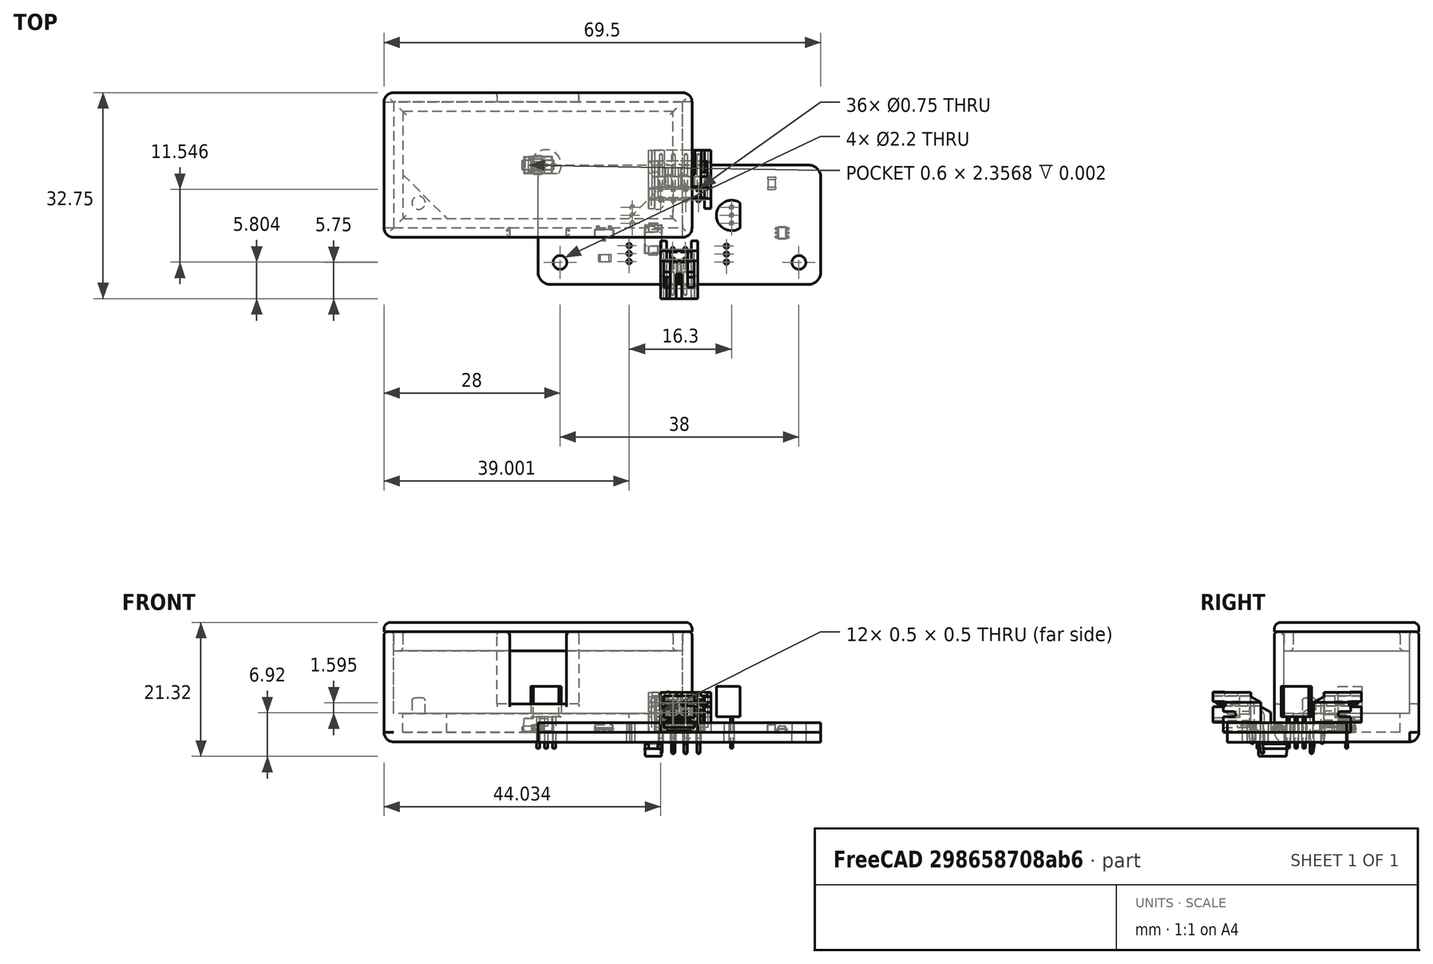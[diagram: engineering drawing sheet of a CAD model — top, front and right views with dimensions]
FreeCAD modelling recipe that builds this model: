
FCSTD DOCUMENT  (FreeCAD 1.0R39319 (Git))
Label: Test2
License: All rights reserved
LicenseURL: https://en.wikipedia.org/wiki/All_rights_reserved
objects: App::Link×31, Part::Feature×18, Sketcher::SketchObject×10, PartDesign::Fillet×8, PartDesign::Pad×6, App::Part×5, PartDesign::Pocket×3, PartDesign::Body×2, Mesh::Feature×2, PartDesign::Thickness×1, PartDesign::CoordinateSystem×1, PartDesign::ShapeBinder×1, App::LinkGroup×1
note: 96 computed .brp shape members not serialized (recipe doc carries the construction recipe); baked Part::Feature solids carry a one-line shape summary decoded from their .brp

FEATURE [Sketcher::SketchObject] Sketch
  ArcFitTolerance = 1e-06
  AttachmentSupport = -> [XY_Plane]
  FullyConstrained = true
  MakeInternals = false
  MapMode = 5
  sketch-geometry (4):
    g0: LineSegment StartX=-23 StartY=10 StartZ=0 EndX=-23 EndY=-10 EndZ=0
    g1: LineSegment StartX=-23 StartY=-10 StartZ=0 EndX=23 EndY=-10 EndZ=0
    g2: LineSegment StartX=23 StartY=-10 StartZ=0 EndX=23 EndY=10 EndZ=0
    g3: LineSegment StartX=23 StartY=10 StartZ=0 EndX=-23 EndY=10 EndZ=0
  constraints (11):
    c: Coincident(g0,g1)
    c: Coincident(g1,g2)
    c: Coincident(g2,g3)
    c: Coincident(g3,g0)
    c: Vertical(g0)
    c: Vertical(g2)
    c: Horizontal(g1)
    c: Horizontal(g3)
    c: Distance(g0,g2) = 46
    c: Distance(g1,g3) = 20
    c: Symmetric(g0,g1,g-1)
FEATURE [PartDesign::Pad] Pad  label="Gehäuse"
  Direction = (0,0,1)
  Length = 16
  Length2 = 10
  Profile = -> Sketch
  ReferenceAxis = -> Sketch [N_Axis]
  Refine = true
  Suppressed = false
  Type = 0
FEATURE [PartDesign::Thickness] Thickness
  Base = -> Pad [Face6]
  BaseFeature = -> Pad
  Intersection = false
  Join = 0
  Mode = 0
  Refine = true
  SupportTransform = false
  Suppressed = false
  Value = 1.5
FEATURE [PartDesign::CoordinateSystem] Local_CS_144d
  AttacherType = Attacher::AttachEngine3D
  MapMode = 2
FEATURE [Part::Feature] Pcb_144d
  Placement = pos=(-88.4,49.6,0) rot=(0,0,1;0rad)
  shape: bbox 45 x 19 x 1.6 mm, 30 faces (baked)
FEATURE [Sketcher::SketchObject] PCB_Sketch_144d
  ArcFitTolerance = 1e-06
  FullyConstrained = false
  MakeInternals = false
  sketch-geometry (8):
    g0: LineSegment StartX=45 StartY=-2 StartZ=0 EndX=45 EndY=-17 EndZ=0
    g1: LineSegment StartX=2 StartY=0 StartZ=0 EndX=43 EndY=0 EndZ=0
    g2: LineSegment StartX=4e-16 StartY=-17 StartZ=0 EndX=0 EndY=-2 EndZ=0
    g3: LineSegment StartX=43 StartY=-19 StartZ=0 EndX=2 EndY=-19 EndZ=0
    g4: ArcOfCircle CenterX=2 CenterY=-17 CenterZ=0 NormalX=0 NormalY=0 NormalZ=-1 AngleXU=-1.5708 Radius=2 StartAngle=0 EndAngle=1.5708
    g5: ArcOfCircle CenterX=2 CenterY=-2 CenterZ=0 NormalX=0 NormalY=0 NormalZ=-1 AngleXU=-7.47076e-07 Radius=2 StartAngle=0 EndAngle=1.5708
    g6: ArcOfCircle CenterX=43 CenterY=-17 CenterZ=0 NormalX=0 NormalY=0 NormalZ=-1 AngleXU=3.14159 Radius=2 StartAngle=0 EndAngle=1.5708
    g7: ArcOfCircle CenterX=43 CenterY=-2 CenterZ=0 NormalX=0 NormalY=0 NormalZ=-1 AngleXU=1.5708 Radius=2 StartAngle=0 EndAngle=1.5708
  constraints (8):
    c: Coincident(g2,g4)
    c: Coincident(g2,g5)
    c: Coincident(g3,g4)
    c: Coincident(g1,g5)
    c: Coincident(g3,g6)
    c: Coincident(g1,g7)
    c: Coincident(g0,g6)
    c: Coincident(g0,g7)
FEATURE [App::Part] Board_Geoms_144d
  Group = -> [Pcb_144d,PCB_Sketch_144d]
  Origin = -> Origin001
FEATURE [Part::Feature] Shape  label="C3_C_0805_2012Metric_59d8a5b28aa1"
  Placement = pos=(37.1791,-2.90075,0) rot=(0,0,-1;1.5708rad)
  shape: bbox 1.25 x 2 x 1.25 mm, 28 faces (baked)
FEATURE [Part::Feature] Shape001  label="Qr1_TO-92_Inline_Narrow_4c17e51feb58"
  Placement = pos=(30.8,-9.3,0) rot=(0,0,1;1.5708rad)
  shape: bbox 3.745 x 4.83 x 9.8 mm, 19 faces (baked)
FEATURE [Part::Feature] Shape002  label="R13_R_0805_2012Metric_05bb72eddab1"
  Placement = pos=(10.6384,-14.7978,0) rot=(0,0,1;0rad)
  shape: bbox 2 x 1.2 x 0.45 mm, 26 faces (baked)
FEATURE [App::Link] R13_R_0805_2012Metric_05bb72eddab1_ln_  label="R12_R_0805_2012Metric_2ca491163d3f"
  LinkPlacement = pos=(41.5,-7.05646,0) rot=(0,0,1;3.14159rad)
  LinkedObject = -> Shape002
  Placement = pos=(41.5,-7.05646,0) rot=(0,0,1;3.14159rad)
FEATURE [App::Link] R13_R_0805_2012Metric_05bb72eddab1_ln_001  label="R7_R_0805_2012Metric_16cffab84ef1"
  LinkPlacement = pos=(6.4,-7.5,0) rot=(0,0,1;1.5708rad)
  LinkedObject = -> Shape002
  Placement = pos=(6.4,-7.5,0) rot=(0,0,1;1.5708rad)
FEATURE [App::Link] R13_R_0805_2012Metric_05bb72eddab1_ln_002  label="R11_R_0805_2012Metric_7a0705619217"
  LinkPlacement = pos=(3.5,-7.1,0) rot=(0,0,1;0rad)
  LinkedObject = -> Shape002
  Placement = pos=(3.5,-7.1,0) rot=(0,0,1;0rad)
FEATURE [Part::Feature] Shape003  label="J2_JST_S2B_PH_K_70a5548a03dd"
  Placement = pos=(21.4384,-13.3978,0) rot=(0,0,1;0rad)
  shape: bbox 5.9 x 7.6 x 8.25 mm, 110 faces (baked)
FEATURE [App::Link] C3_C_0805_2012Metric_59d8a5b28aa1_ln_  label="C4_C_0805_2012Metric_db03d5f05126"
  LinkPlacement = pos=(41.6791,-2.90075,0) rot=(0,0,-1;1.5708rad)
  LinkedObject = -> Shape
  Placement = pos=(41.6791,-2.90075,0) rot=(0,0,-1;1.5708rad)
FEATURE [Part::Feature] Shape004  label="D1_SOT-23_6e08a76b6de6"
  Placement = pos=(10.5,-10.8978,0) rot=(0,0,-1;1.5708rad)
  shape: bbox 3 x 2.5 x 1.2 mm, 69 faces (baked)
FEATURE [App::Link] R13_R_0805_2012Metric_05bb72eddab1_ln_003  label="R1_R_0805_2012Metric_524cef724ac0"
  LinkPlacement = pos=(5.02083,-2.90344,0) rot=(0,0,-1;1.5708rad)
  LinkedObject = -> Shape002
  Placement = pos=(5.02083,-2.90344,0) rot=(0,0,-1;1.5708rad)
FEATURE [App::Link] R13_R_0805_2012Metric_05bb72eddab1_ln_004  label="R14_R_0805_2012Metric_7cf8be774751"
  LinkPlacement = pos=(34.7,-14.8,0) rot=(0,0,1;0rad)
  LinkedObject = -> Shape002
  Placement = pos=(34.7,-14.8,0) rot=(0,0,1;0rad)
FEATURE [App::Link] Qr1_TO_92_Inline_Narrow_4c17e51feb58_ln_  label="Ql1_TO-92_Inline_Narrow_06a0bbdb9195"
  LinkPlacement = pos=(15,-9.3,0) rot=(0,0,1;1.5708rad)
  LinkedObject = -> Shape001
  Placement = pos=(15,-9.3,0) rot=(0,0,1;1.5708rad)
FEATURE [App::Link] R13_R_0805_2012Metric_05bb72eddab1_ln_005  label="R10_R_0805_2012Metric_43a2ade0cd3b"
  LinkPlacement = pos=(38.6,-7.4,0) rot=(0,0,1;1.5708rad)
  LinkedObject = -> Shape002
  Placement = pos=(38.6,-7.4,0) rot=(0,0,1;1.5708rad)
FEATURE [Part::Feature] Shape005  label="Q2_SOT-363_SC-70-6_a433c7552343"
  Placement = pos=(38.8384,-10.7978,0) rot=(0,0,1;0rad)
  shape: bbox 2.1 x 2 x 1.05 mm, 111 faces (baked)
FEATURE [App::Link] R13_R_0805_2012Metric_05bb72eddab1_ln_006  label="R5_R_0805_2012Metric_740ab295292b"
  LinkPlacement = pos=(34.9791,-2.93075,0) rot=(0,0,-1;1.5708rad)
  LinkedObject = -> Shape002
  Placement = pos=(34.9791,-2.93075,0) rot=(0,0,-1;1.5708rad)
FEATURE [App::Link] R13_R_0805_2012Metric_05bb72eddab1_ln_007  label="R8_R_0805_2012Metric_f95ea44c56ff"
  LinkPlacement = pos=(9.3,-7.05784,0) rot=(0,0,1;0rad)
  LinkedObject = -> Shape002
  Placement = pos=(9.3,-7.05784,0) rot=(0,0,1;0rad)
FEATURE [App::Link] R13_R_0805_2012Metric_05bb72eddab1_ln_008  label="R4_R_0805_2012Metric_864b704fb597"
  LinkPlacement = pos=(32.7384,-2.93075,0) rot=(0,0,1;1.5708rad)
  LinkedObject = -> Shape002
  Placement = pos=(32.7384,-2.93075,0) rot=(0,0,1;1.5708rad)
FEATURE [App::Link] D1_SOT_23_6e08a76b6de6_ln_  label="D2_SOT-23_9dcc648aeed5"
  LinkPlacement = pos=(34.6,-10.9978,0) rot=(0,0,1;1.5708rad)
  LinkedObject = -> Shape004
  Placement = pos=(34.6,-10.9978,0) rot=(0,0,1;1.5708rad)
FEATURE [App::Link] R13_R_0805_2012Metric_05bb72eddab1_ln_009  label="R6_R_0805_2012Metric_ad0c409fa7e4"
  LinkPlacement = pos=(39.4791,-2.93075,0) rot=(0,0,-1;1.5708rad)
  LinkedObject = -> Shape002
  Placement = pos=(39.4791,-2.93075,0) rot=(0,0,-1;1.5708rad)
FEATURE [App::Link] C3_C_0805_2012Metric_59d8a5b28aa1_ln_001  label="C1_C_0805_2012Metric_d2daac75df9f"
  LinkPlacement = pos=(2.82083,-2.93343,0) rot=(0,0,-1;1.5708rad)
  LinkedObject = -> Shape
  Placement = pos=(2.82083,-2.93343,0) rot=(0,0,-1;1.5708rad)
FEATURE [App::Link] Q2_SOT_363_SC_70_6_a433c7552343_ln_  label="Q1_SOT-363_SC-70-6_3db5755c4068"
  LinkPlacement = pos=(6.23841,-10.7978,0) rot=(0,0,1;0rad)
  LinkedObject = -> Shape005
  Placement = pos=(6.23841,-10.7978,0) rot=(0,0,1;0rad)
FEATURE [Part::Feature] Shape006  label="J1_JST_S4B_PH_K_9acb058e8168"
  Placement = pos=(25.5335,-5.59784,0) rot=(0,0,1;3.14159rad)
  shape: bbox 9.9 x 7.6 x 8.25 mm, 174 faces (baked)
FEATURE [App::Link] C3_C_0805_2012Metric_59d8a5b28aa1_ln_002  label="C2_C_0805_2012Metric_59fbecc238c2"
  LinkPlacement = pos=(7.28708,-2.93343,0) rot=(0,0,-1;1.5708rad)
  LinkedObject = -> Shape
  Placement = pos=(7.28708,-2.93343,0) rot=(0,0,-1;1.5708rad)
FEATURE [App::Link] Qr1_TO_92_Inline_Narrow_4c17e51feb58_ln_001  label="Qr2_TO-92_Inline_Narrow_77d01d929e14"
  LinkPlacement = pos=(29.974,-12.9064,0) rot=(0,0,-1;1.5708rad)
  LinkedObject = -> Shape001
  Placement = pos=(29.974,-12.9064,0) rot=(0,0,-1;1.5708rad)
FEATURE [App::Link] Qr1_TO_92_Inline_Narrow_4c17e51feb58_ln_002  label="Ql2_TO-92_Inline_Narrow_95b5c1c7d89b"
  LinkPlacement = pos=(14.5005,-12.8254,0) rot=(0,0,-1;1.5708rad)
  LinkedObject = -> Shape001
  Placement = pos=(14.5005,-12.8254,0) rot=(0,0,-1;1.5708rad)
FEATURE [App::Link] R13_R_0805_2012Metric_05bb72eddab1_ln_010  label="R2_R_0805_2012Metric_44288069eabb"
  LinkPlacement = pos=(9.48708,-2.90344,0) rot=(0,0,-1;1.5708rad)
  LinkedObject = -> Shape002
  Placement = pos=(9.48708,-2.90344,0) rot=(0,0,-1;1.5708rad)
FEATURE [App::Link] R13_R_0805_2012Metric_05bb72eddab1_ln_011  label="R3_R_0805_2012Metric_4998b09c78f7"
  LinkPlacement = pos=(11.8384,-2.93343,0) rot=(0,0,1;1.5708rad)
  LinkedObject = -> Shape002
  Placement = pos=(11.8384,-2.93343,0) rot=(0,0,1;1.5708rad)
FEATURE [App::Link] R13_R_0805_2012Metric_05bb72eddab1_ln_012  label="R9_R_0805_2012Metric_5794d63d1f74"
  LinkPlacement = pos=(35.6902,-7.05646,0) rot=(0,0,1;0rad)
  LinkedObject = -> Shape002
  Placement = pos=(35.6902,-7.05646,0) rot=(0,0,1;0rad)
FEATURE [App::Part] Top_144d
  Group = -> [Shape,Shape001,Shape002,R13_R_0805_2012Metric_05bb72eddab1_ln_,R13_R_0805_2012Metric_05bb72eddab1_ln_001,R13_R_0805_2012Metric_05bb72eddab1_ln_002,Shape003,C3_C_0805_2012Metric_59d8a5b28aa1_ln_,Shape004,R13_R_0805_2012Metric_05bb72eddab1_ln_003,R13_R_0805_2012Metric_05bb72eddab1_ln_004,Qr1_TO_92_Inline_Narrow_4c17e51feb58_ln_,R13_R_0805_2012Metric_05bb72eddab1_ln_005,Shape005,+14 more]
  Origin = -> Origin004
FEATURE [Part::Feature] Shape007  label="D6_D_SMA_e8e529742dff"
  Placement = pos=(18.3384,-11.7978,-1.6) rot=(0.707107,-0.707107,0;3.14159rad)
  shape: bbox 2.7 x 5 x 2.22 mm, 41 faces (baked)
FEATURE [App::Link] C3_C_0805_2012Metric_59d8a5b28aa1_ln_003  label="C5_C_0805_2012Metric_b10809d84286"
  LinkPlacement = pos=(28.2,-4.8,-1.6) rot=(0.707107,0.707107,0;3.14159rad)
  LinkedObject = -> Shape
  Placement = pos=(28.2,-4.8,-1.6) rot=(0.707107,0.707107,0;3.14159rad)
FEATURE [App::Link] D6_D_SMA_e8e529742dff_ln_  label="D5_D_SMA_a7689d39181a"
  LinkPlacement = pos=(26.5884,-11.7978,-1.6) rot=(0.707107,-0.707107,0;3.14159rad)
  LinkedObject = -> Shape007
  Placement = pos=(26.5884,-11.7978,-1.6) rot=(0.707107,-0.707107,0;3.14159rad)
FEATURE [App::Link] D6_D_SMA_e8e529742dff_ln_001  label="D4_D_SMA_3d6ee32131fe"
  LinkPlacement = pos=(10.9305,-8.73034,-1.6) rot=(0.707107,0.707107,0;3.14159rad)
  LinkedObject = -> Shape007
  Placement = pos=(10.9305,-8.73034,-1.6) rot=(0.707107,0.707107,0;3.14159rad)
FEATURE [App::Link] D6_D_SMA_e8e529742dff_ln_002  label="D3_D_SMA_7099b9f5290d"
  LinkPlacement = pos=(34.134,-8.73034,-1.6) rot=(0.707107,0.707107,0;3.14159rad)
  LinkedObject = -> Shape007
  Placement = pos=(34.134,-8.73034,-1.6) rot=(0.707107,0.707107,0;3.14159rad)
FEATURE [App::Part] Bot_144d
  Group = -> [Shape007,C3_C_0805_2012Metric_59d8a5b28aa1_ln_003,D6_D_SMA_e8e529742dff_ln_,D6_D_SMA_e8e529742dff_ln_001,D6_D_SMA_e8e529742dff_ln_002]
  Origin = -> Origin005
FEATURE [App::Part] Step_Models_144d
  Group = -> [Top_144d,Bot_144d]
  Origin = -> Origin003
FEATURE [App::Part] Board_144d  label="npn-pnp-h-bridge"
  Group = -> [Local_CS_144d,Board_Geoms_144d,Step_Models_144d]
  Origin = -> Origin002
  Placement = pos=(-22.5,9.5,4.5) rot=(0,0,1;0rad)
FEATURE [Sketcher::SketchObject] Sketch001  label="pcb-base"
  ArcFitTolerance = 1e-06
  AttachmentSupport = -> [XY_Plane]
  ExternalGeometry = -> [Thickness]
  FullyConstrained = true
  MakeInternals = false
  MapMode = 5
  sketch-geometry (14):
    g0: LineSegment StartX=-23 StartY=10 StartZ=0 EndX=-23 EndY=-10 EndZ=0
    g1: LineSegment StartX=-23 StartY=-10 StartZ=0 EndX=23 EndY=-10 EndZ=0
    g2: LineSegment StartX=23 StartY=-10 StartZ=0 EndX=23 EndY=10 EndZ=0
    g3: LineSegment StartX=23 StartY=10 StartZ=0 EndX=-23 EndY=10 EndZ=0
    g4: LineSegment StartX=-21.5 StartY=8.5 StartZ=0 EndX=-21.5 EndY=-1.51 EndZ=0
    g5: LineSegment StartX=-14.51 StartY=-8.5 StartZ=0 EndX=14.51 EndY=-8.5 EndZ=0
    g6: LineSegment StartX=21.5 StartY=-1.51 StartZ=0 EndX=21.5 EndY=8.5 EndZ=0
    g7: LineSegment StartX=21.5 StartY=8.5 StartZ=0 EndX=-21.5 EndY=8.5 EndZ=0
    g8: ArcOfCircle [constr] CenterX=-14.51 CenterY=-1.51 CenterZ=0 NormalX=0 NormalY=0 NormalZ=1 AngleXU=0 Radius=6.99 StartAngle=3.14159 EndAngle=4.71239
    g9: GeomPoint [constr] X=-21.5 Y=-8.5 Z=0
    g10: LineSegment StartX=-21.5 StartY=-1.51 StartZ=0 EndX=-14.51 EndY=-8.5 EndZ=0
    g11: ArcOfCircle [constr] CenterX=14.51 CenterY=-1.51 CenterZ=0 NormalX=0 NormalY=0 NormalZ=1 AngleXU=0 Radius=6.99 StartAngle=4.71239 EndAngle=6.28319
    g12: GeomPoint [constr] X=21.5 Y=-8.5 Z=0
    g13: LineSegment StartX=14.51 StartY=-8.5 StartZ=0 EndX=21.5 EndY=-1.51 EndZ=0
  constraints (32):
    c: Coincident(g0,g1)
    c: Coincident(g1,g2)
    c: Coincident(g2,g3)
    c: Coincident(g3,g0)
    c: Vertical(g0)
    c: Vertical(g2)
    c: Horizontal(g1)
    c: Horizontal(g3)
    c: Coincident(g0,g-5)
    c: Coincident(g1,g-6)
    c: Coincident(g6,g7)
    c: Coincident(g7,g4)
    c: Vertical(g4)
    c: Vertical(g6)
    c: Horizontal(g5)
    c: Horizontal(g7)
    c: Distance(g4,g6) = 43
    c: Distance(g9,g7) = 17
    c: Symmetric(g4,g12,g-1)
    c: PointOnObject(g9,g4)
    c: PointOnObject(g9,g5)
    c: Tangent(g4,g8) = -1.5708
    c: Tangent(g5,g8) = -1.5708
    c: Coincident(g10,g4)
    c: Coincident(g10,g5)
    c: PointOnObject(g12,g5)
    c: Tangent(g5,g11) = -1.5708
    c: Tangent(g6,g11) = -1.5708
    c: Coincident(g13,g5)
    c: Coincident(g13,g6)
    c: Symmetric(g8,g11,g-2)
    c: DistanceX(g-1,g11) = 14.51
FEATURE [PartDesign::Pad] Pad001  label="PCB-Base"
  BaseFeature = -> Thickness
  Direction = (0,0,1)
  Length = 3
  Length2 = 10
  Profile = -> Sketch001
  ReferenceAxis = -> Sketch001 [N_Axis]
  Refine = true
  Suppressed = false
  Type = 0
FEATURE [PartDesign::Pad] Pad002
  BaseFeature = -> Pad001
  Direction = (0,0,1)
  Length = 3
  Length2 = 10
  Profile = -> Sketch001
  ReferenceAxis = -> Sketch001 [N_Axis]
  Refine = true
  Suppressed = false
  Type = 0
FEATURE [Sketcher::SketchObject] Sketch002
  ArcFitTolerance = 1e-06
  AttachmentSupport = -> [XY_Plane]
  ExternalGeometry = -> [Pad002]
  FullyConstrained = true
  MakeInternals = false
  MapMode = 5
  sketch-geometry (2):
    g0: Circle CenterX=-19 CenterY=-6 CenterZ=0 NormalX=0 NormalY=0 NormalZ=1 AngleXU=0 Radius=1.05
    g1: Circle CenterX=19 CenterY=-6 CenterZ=0 NormalX=0 NormalY=0 NormalZ=1 AngleXU=0 Radius=1.05
  constraints (6):
    c: Diameter(g0) = 2.1
    c: Diameter(g1) = 2.1
    c: DistanceX(g-3,g0) = 4
    c: DistanceY(g-3,g0) = 4
    c: DistanceY(g-4,g1) = 4
    c: DistanceX(g1,g-6) = 4
FEATURE [PartDesign::Pad] Pad003  label="Nubsis"
  BaseFeature = -> Pad002
  Direction = (0,0,1)
  Length = 5.5
  Length2 = 10
  Profile = -> Sketch002
  ReferenceAxis = -> Sketch002 [N_Axis]
  Refine = true
  Suppressed = false
  Type = 0
FEATURE [Sketcher::SketchObject] Sketch003
  ArcFitTolerance = 1e-06
  AttachmentSupport = -> [Pad003]
  ExternalGeometry = -> [Pad003]
  FullyConstrained = true
  MakeInternals = false
  MapMode = 5
  Placement = pos=(0,-11.5,0) rot=(1,0,0;1.5708rad)
  sketch-geometry (4):
    g0: LineSegment StartX=4.5 StartY=24.55 StartZ=0 EndX=-4.5 EndY=24.55 EndZ=0
    g1: LineSegment StartX=-4.5 StartY=24.55 StartZ=0 EndX=-4.5 EndY=4.55 EndZ=0
    g2: LineSegment StartX=-4.5 StartY=4.55 StartZ=0 EndX=4.5 EndY=4.55 EndZ=0
    g3: LineSegment StartX=4.5 StartY=4.55 StartZ=0 EndX=4.5 EndY=24.55 EndZ=0
  constraints (12):
    c: Coincident(g0,g1)
    c: Coincident(g1,g2)
    c: Coincident(g2,g3)
    c: Coincident(g3,g0)
    c: Horizontal(g0)
    c: Horizontal(g2)
    c: Vertical(g1)
    c: Vertical(g3)
    c: Distance(g1,g3) = 9
    c: Distance(g0,g2) = 20
    c: DistanceY(g1,g-3) = -4.55
    c: DistanceX(g0,g-1) = 4.5
FEATURE [PartDesign::Pocket] Pocket  label="Pocket S2B"
  BaseFeature = -> Pad003
  Direction = (0,1,-2e-16)
  Length = 1.5
  Length2 = 5
  Profile = -> Sketch003
  ReferenceAxis = -> Sketch003 [N_Axis]
  Refine = true
  Suppressed = false
  Type = 0
FEATURE [Sketcher::SketchObject] Sketch004
  ArcFitTolerance = 1e-06
  AttachmentSupport = -> [Pocket]
  ExternalGeometry = -> [Pocket]
  FullyConstrained = false
  MakeInternals = false
  MapMode = 5
  Placement = pos=(0,11.5,0) rot=(0,0.707107,0.707107;3.14159rad)
  sketch-geometry (4):
    g0: LineSegment StartX=-6.5 StartY=24.55 StartZ=0 EndX=-6.5 EndY=4.55 EndZ=0
    g1: LineSegment StartX=-6.5 StartY=4.55 StartZ=0 EndX=6.5 EndY=4.55 EndZ=0
    g2: LineSegment StartX=6.5 StartY=4.55 StartZ=0 EndX=6.5 EndY=24.55 EndZ=0
    g3: LineSegment StartX=6.5 StartY=24.55 StartZ=0 EndX=-6.5 EndY=24.55 EndZ=0
  constraints (11):
    c: Coincident(g0,g1)
    c: Coincident(g1,g2)
    c: Coincident(g2,g3)
    c: Coincident(g3,g0)
    c: Vertical(g0)
    c: Vertical(g2)
    c: Horizontal(g1)
    c: Horizontal(g3)
    c: Distance(g0,g2) = 13
    c: Distance(g1,g3) = 20
    c: DistanceY(g0,g-3) = -4.55
FEATURE [PartDesign::Pocket] Pocket001  label="Pocket S4b"
  BaseFeature = -> Pocket
  Direction = (0,-1,2e-16)
  Length = 1.5
  Length2 = 5
  Profile = -> Sketch004
  ReferenceAxis = -> Sketch004 [N_Axis]
  Refine = true
  Suppressed = false
  Type = 0
FEATURE [PartDesign::ShapeBinder] CopyPocket001
  Placement = pos=(0,0,15) rot=(0,0,1;0rad)
  TraceSupport = false
FEATURE [Sketcher::SketchObject] Sketch005
  ArcFitTolerance = 1e-06
  AttachmentSupport = -> [CopyPocket001]
  FullyConstrained = true
  MakeInternals = false
  MapMode = 5
  Placement = pos=(0,0,15) rot=(0,0,1;0rad)
  expr: Constraints[8] = 46 mm - 0.05 mm
  expr: Constraints[9] = 20 mm - 0.05 mm
  sketch-geometry (4):
    g0: LineSegment StartX=-22.975 StartY=9.975 StartZ=0 EndX=-22.975 EndY=-9.975 EndZ=0
    g1: LineSegment StartX=-22.975 StartY=-9.975 StartZ=0 EndX=22.975 EndY=-9.975 EndZ=0
    g2: LineSegment StartX=22.975 StartY=-9.975 StartZ=0 EndX=22.975 EndY=9.975 EndZ=0
    g3: LineSegment StartX=22.975 StartY=9.975 StartZ=0 EndX=-22.975 EndY=9.975 EndZ=0
  constraints (11):
    c: Coincident(g0,g1)
    c: Coincident(g1,g2)
    c: Coincident(g2,g3)
    c: Coincident(g3,g0)
    c: Vertical(g0)
    c: Vertical(g2)
    c: Horizontal(g1)
    c: Horizontal(g3)
    c: Distance(g0,g2) = 45.95
    c: Distance(g1,g3) = 19.95
    c: Symmetric(g0,g1,g-1)
FEATURE [PartDesign::Pad] Pad004  label="Kante Deckelinnenseite"
  Direction = (0,0,1)
  Length = 3
  Length2 = 10
  Placement = pos=(0,0,15) rot=(0,0,1;0rad)
  Profile = -> Sketch005
  ReferenceAxis = -> Sketch005 [N_Axis]
  Refine = true
  Reversed = true
  Suppressed = false
  Type = 0
FEATURE [Sketcher::SketchObject] Sketch006
  ArcFitTolerance = 1e-06
  AttachmentSupport = -> [Pad004]
  FullyConstrained = true
  MakeInternals = false
  MapMode = 5
  Placement = pos=(0,0,15) rot=(0,0,1;0rad)
  sketch-geometry (4):
    g0: LineSegment StartX=-21.5 StartY=8.5 StartZ=0 EndX=-21.5 EndY=-8.5 EndZ=0
    g1: LineSegment StartX=-21.5 StartY=-8.5 StartZ=0 EndX=21.5 EndY=-8.5 EndZ=0
    g2: LineSegment StartX=21.5 StartY=-8.5 StartZ=0 EndX=21.5 EndY=8.5 EndZ=0
    g3: LineSegment StartX=21.5 StartY=8.5 StartZ=0 EndX=-21.5 EndY=8.5 EndZ=0
  constraints (11):
    c: Coincident(g0,g1)
    c: Coincident(g1,g2)
    c: Coincident(g2,g3)
    c: Coincident(g3,g0)
    c: Vertical(g0)
    c: Vertical(g2)
    c: Horizontal(g1)
    c: Horizontal(g3)
    c: DistanceX(g3,g3) = 43
    c: DistanceY(g0,g0) = 17
    c: Symmetric(g0,g1,g-1)
FEATURE [PartDesign::Pocket] Pocket002
  BaseFeature = -> Pad004
  Direction = (0,0,-1)
  Length = 5
  Length2 = 5
  Placement = pos=(0,0,15) rot=(0,0,1;0rad)
  Profile = -> Sketch006
  ReferenceAxis = -> Sketch006 [N_Axis]
  Refine = true
  Suppressed = false
  Type = 0
FEATURE [Sketcher::SketchObject] Sketch007
  ArcFitTolerance = 1e-06
  AttachmentSupport = -> [Pocket002]
  FullyConstrained = true
  MakeInternals = false
  MapMode = 5
  Placement = pos=(0,0,15) rot=(0,0,1;0rad)
  sketch-geometry (4):
    g0: LineSegment StartX=-24.5 StartY=11.5 StartZ=0 EndX=-24.5 EndY=-11.5 EndZ=0
    g1: LineSegment StartX=-24.5 StartY=-11.5 StartZ=0 EndX=24.5 EndY=-11.5 EndZ=0
    g2: LineSegment StartX=24.5 StartY=-11.5 StartZ=0 EndX=24.5 EndY=11.5 EndZ=0
    g3: LineSegment StartX=24.5 StartY=11.5 StartZ=0 EndX=-24.5 EndY=11.5 EndZ=0
  constraints (11):
    c: Coincident(g0,g1)
    c: Coincident(g1,g2)
    c: Coincident(g2,g3)
    c: Coincident(g3,g0)
    c: Vertical(g0)
    c: Vertical(g2)
    c: Horizontal(g1)
    c: Horizontal(g3)
    c: Distance(g0,g2) = 49
    c: Distance(g1,g3) = 23
    c: Symmetric(g0,g1,g-1)
FEATURE [PartDesign::Pad] Pad005
  BaseFeature = -> Pocket002
  Direction = (0,0,1)
  Length = 1.5
  Length2 = 10
  Placement = pos=(0,0,15) rot=(0,0,1;0rad)
  Profile = -> Sketch007
  ReferenceAxis = -> Sketch007 [N_Axis]
  Refine = true
  Suppressed = false
  Type = 0
FEATURE [PartDesign::Fillet] Fillet
  Base = -> Pad005 [Edge22,Edge21,Edge26,Edge24]
  BaseFeature = -> Pad005
  Placement = pos=(0,0,15) rot=(0,0,1;0rad)
  Radius = 1.5
  Refine = true
  SupportTransform = false
  Suppressed = false
  UseAllEdges = false
FEATURE [PartDesign::Fillet] Fillet001
  Base = -> Fillet [Edge27]
  BaseFeature = -> Fillet
  Placement = pos=(0,0,15) rot=(0,0,1;0rad)
  Radius = 1
  Refine = true
  SupportTransform = false
  Suppressed = false
  UseAllEdges = false
FEATURE [PartDesign::Fillet] Fillet006  label="Rundung Base"
  Base = -> Pocket001 [Edge6]
  BaseFeature = -> Pocket001
  Radius = 0.5
  Refine = true
  SupportTransform = false
  Suppressed = false
  UseAllEdges = false
FEATURE [PartDesign::Fillet] Fillet007  label="Rundung Nubsis"
  Base = -> Fillet006 [Face28,Face29]
  BaseFeature = -> Fillet006
  Radius = 0.5
  Refine = true
  SupportTransform = false
  Suppressed = false
  UseAllEdges = false
FEATURE [PartDesign::Fillet] Fillet008  label="Rundung Kanten Löcher Unten"
  Base = -> Fillet007 [Edge74,Edge60]
  BaseFeature = -> Fillet007
  Radius = 0.5
  Refine = true
  SupportTransform = false
  Suppressed = false
  UseAllEdges = false
FEATURE [PartDesign::Fillet] Fillet009  label="Rundung Kanten Löcher"
  Base = -> Fillet008 [Edge65,Edge63]
  BaseFeature = -> Fillet008
  Radius = 0.2
  Refine = true
  SupportTransform = false
  Suppressed = false
  UseAllEdges = false
FEATURE [PartDesign::Fillet] Fillet010  label="Rundung Oberkante"
  Base = -> Fillet009 [Edge6,Edge62,Edge12,Edge16,Edge1,Edge10,Edge8,Edge3,Edge11,Edge9,Edge5,Edge52,Edge34,Edge64,Edge63,Edge61,Edge41]
  BaseFeature = -> Fillet009
  Radius = 0.5
  Refine = true
  SupportTransform = false
  Suppressed = false
  UseAllEdges = false
FEATURE [PartDesign::Body] Body
  AllowCompound = false
  Group = -> [Sketch,Pad,Thickness,Sketch001,Pad001,Pad002,Sketch002,Pad003,Sketch003,Pocket,Sketch004,Pocket001,Fillet006,Fillet007,Fillet008,Fillet009,Fillet010]
  Origin = -> Origin
  Tip = -> Fillet010
FEATURE [Part::Feature] Solid  label="C_0805_2012Metric"
  shape: bbox 2 x 1.25 x 1.25 mm, 28 faces (baked)
FEATURE [Part::Feature] Solid001  label="TO-92_Inline"
  shape: bbox 4.83 x 3.745 x 9.8 mm, 19 faces (baked)
FEATURE [Part::Feature] Solid002  label="R_0805_2012Metric"
  shape: bbox 2 x 1.2 x 0.45 mm, 26 faces (baked)
FEATURE [Part::Feature] Solid003  label="JST_PH_S2B-PH-K_1x02_P2.00mm_Horizontal"
  Placement = pos=(21.4384,-15,1.595) rot=(0,0,1;0rad)
  shape: bbox 5.9 x 7.6 x 8.25 mm, 110 faces (baked)
FEATURE [Part::Feature] Solid004  label="SOT-23"
  shape: bbox 2.5 x 3 x 1.2 mm, 69 faces (baked)
FEATURE [Part::Feature] Solid005  label="SOT-363_SC-70-6"
  shape: bbox 2.1 x 2 x 1.05 mm, 111 faces (baked)
FEATURE [Part::Feature] Solid006  label="JST_PH_S4B-PH-K_1x04_P2.00mm_Horizontal"
  Placement = pos=(25.5335,-3.9,1.595) rot=(0,0,1;3.14159rad)
  shape: bbox 9.9 x 7.6 x 8.25 mm, 174 faces (baked)
FEATURE [Part::Feature] Solid007  label="D_SMA"
  shape: bbox 5 x 2.7 x 2.22 mm, 41 faces (baked)
FEATURE [Part::Feature] Solid008  label="npn-pnp-h-bridge_PCB"
  shape: bbox 45 x 19 x 1.51 mm, 30 faces (baked)
FEATURE [App::Link] Link  label="C_0805_2012Metric001"
  ElementCount = 5
  LinkedObject = -> Solid
  PlacementList = 5 placements: [(37.1791,-2.90075,1.595),(41.6791,-2.90075,1.595),(2.82083,-2.93343,1.595),(7.28708,-2.93343,1.595),(24.6,-6,-0.085)]
  ScaleList = (5) [(1,1,1),(1,1,1),(1,1,1),(1,1,1),(1,1,1)]
  ShowElement = false
FEATURE [App::Link] Link001  label="TO-92_Inline001"
  ElementCount = 4
  LinkedObject = -> Solid001
  PlacementList = 4 placements: [(30.8,-9.3,1.595),(15,-9.3,1.595),(29.974,-12.9064,1.595),(14.5005,-12.8254,1.595)]
  ScaleList = (4) [(1,1,1),(1,1,1),(1,1,1),(1,1,1)]
  ShowElement = false
FEATURE [App::Link] Link002  label="R_0805_2012Metric001"
  ElementCount = 14
  LinkedObject = -> Solid002
  PlacementList = 14 placements: [(10.6384,-14.7978,1.595),(41.5,-7.05646,1.595),(6.4,-7.5,1.595),(3.5,-7.1,1.595),(5.02083,-2.90343,1.595),(34.7,-14.8,1.595),(38.6,-7.4,1.595),(34.9791,-2.93075,1.595),(9.3,-7.05784,1.595),(32.7384,-2.93075,1.595),(39.4791,-2.93075,1.595),(9.48708,-2.90343,1.595),(11.8384,-2.93343,1.595),(35.6902,-7.05646,1.595)]
  ScaleList = (14) [(1,1,1),(1,1,1),(1,1,1),(1,1,1),(1,1,1),(1,1,1),(1,1,1),(1,1,1),(1,1,1),(1,1,1),(1,1,1),(1,1,1),(1,1,1),(1,1,1)]
  ShowElement = false
FEATURE [App::Link] Link003  label="SOT-024"
  ElementCount = 2
  LinkedObject = -> Solid004
  PlacementList = 2 placements: [(10.5,-10.8978,1.595),(34.6,-10.9978,1.595)]
  ScaleList = (2) [(1,1,1),(1,1,1)]
  ShowElement = false
FEATURE [App::Link] Link004  label="SOT-363_SC-70-007"
  ElementCount = 2
  LinkedObject = -> Solid005
  PlacementList = 2 placements: [(38.8384,-10.7978,1.595),(6.23841,-10.7978,1.595)]
  ScaleList = (2) [(1,1,1),(1,1,1)]
  ShowElement = false
FEATURE [App::Link] Link005  label="D_SMA001"
  ElementCount = 4
  LinkedObject = -> Solid007
  PlacementList = 4 placements: [(18.3384,-11.7978,-0.085),(26.5884,-11.7978,-0.085),(10.9305,-8.73034,-0.085),(34.134,-8.73034,-0.085)]
  ScaleList = (4) [(1,1,1),(1,1,1),(1,1,1),(1,1,1)]
  ShowElement = false
FEATURE [App::LinkGroup] LinkGroup  label="npn-pnp-h-bridge 1"
  ElementList = -> [Link,Link001,Link002,Solid003,Link003,Link004,Solid006,Link005,Solid008]
  LinkMode = 0
  Placement = pos=(-22.5,9.50001,3) rot=(0,0,1;0rad)
FEATURE [PartDesign::Fillet] Fillet012  label="Innenrundung Deckel001"
  Base = -> Fillet001 [Edge56,Edge64,Edge55,Edge62,Edge54,Edge60,Edge57,Edge53,Edge20,Edge19,Edge18,Edge17]
  BaseFeature = -> Fillet001
  Placement = pos=(0,0,15) rot=(0,0,1;0rad)
  Radius = 0.5
  Refine = true
  SupportTransform = false
  Suppressed = false
  UseAllEdges = false
FEATURE [Sketcher::SketchObject] Sketch008
  ArcFitTolerance = 1e-06
  AttachmentSupport = -> [Fillet012]
  FullyConstrained = true
  MakeInternals = false
  MapMode = 5
  Placement = pos=(0,0,15) rot=(1,0,0;3.14159rad)
FEATURE [PartDesign::Body] Body002  label="Deckel"
  AllowCompound = false
  Group = -> [CopyPocket001,Sketch005,Pad004,Sketch006,Pocket002,Sketch007,Pad005,Fillet,Fillet001,Fillet012,Sketch008]
  Origin = -> Origin007
  Placement = pos=(0,0,1) rot=(0,0,1;0rad)
  Tip = -> Fillet012
FEATURE [Mesh::Feature] Mesh  label="Body (Meshed)"
FEATURE [Mesh::Feature] Mesh001  label="Deckel (Meshed)"
